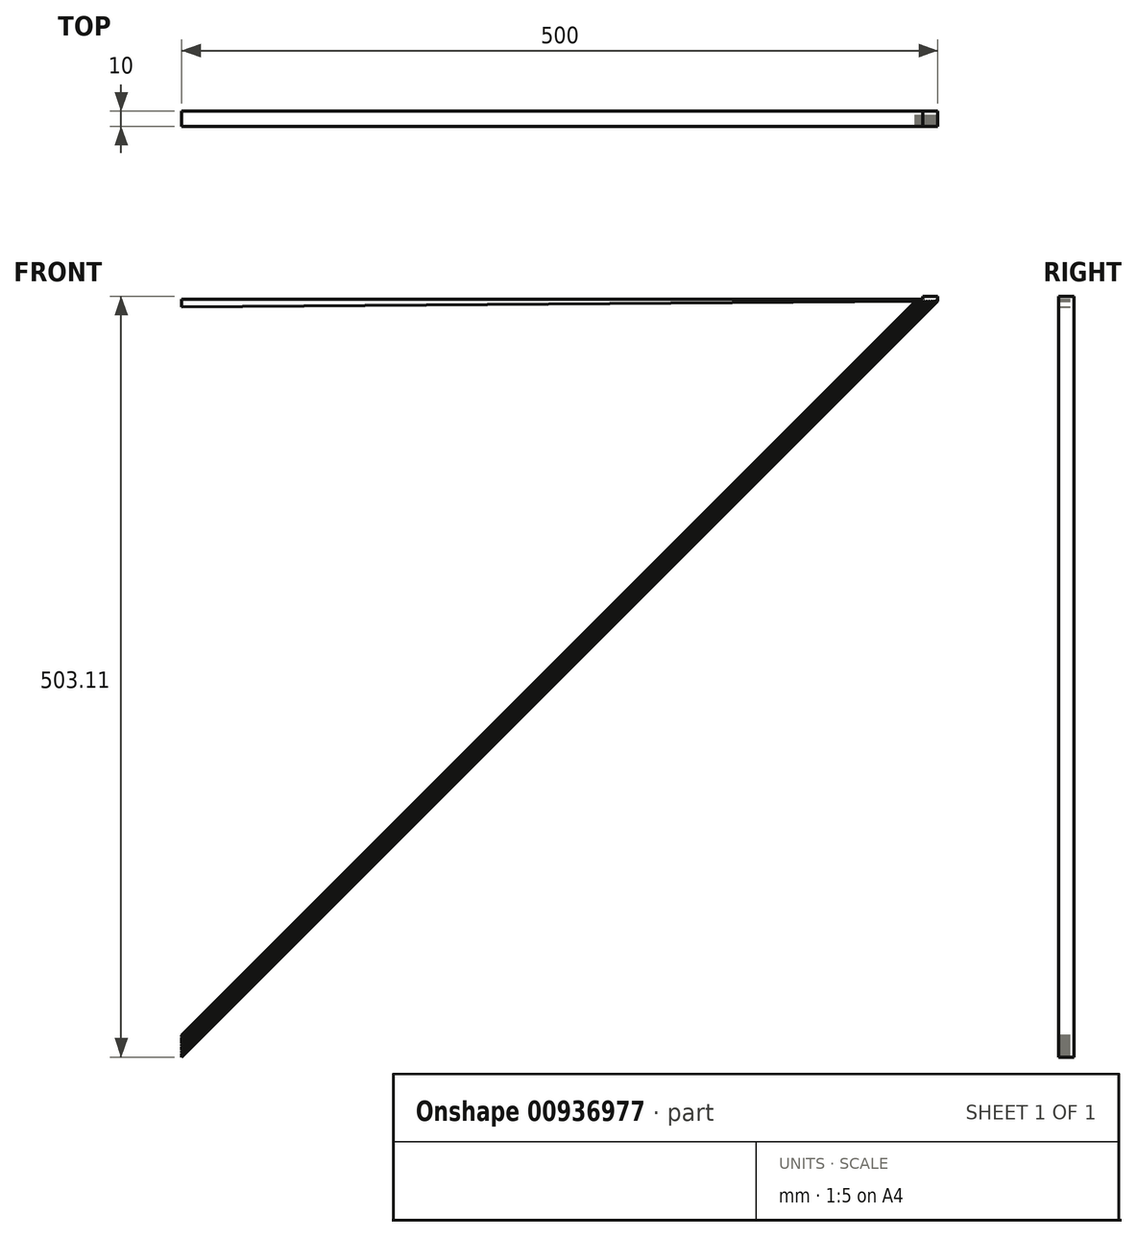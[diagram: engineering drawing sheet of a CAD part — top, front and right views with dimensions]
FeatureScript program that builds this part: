
annotation { "Feature Type Name" : "Feature", "Feature Type Description" : "" }
export const myFeature = defineFeature(function(context is Context, id is Id, definition is map)
    precondition{}
    {
        {
            var Q0;
            Q0=qCreatedBy(makeId("Front.planeOp"),FACE);
            var sketch = newSketch(context, id + "F0", { "sketchPlane" : qUnion([Q0])});
            skLineSegment(sketch, "E0.right", {"start": v(249.85, 318.38) * mm, "end": v(249.85, 317.38) * mm});
            skLineSegment(sketch, "E1", {"start": v(249.85, 318.38) * mm, "end": v(-250.15, 318.38) * mm});
            skLineSegment(sketch, "E2", {"start": v(-250.15, 318.38) * mm, "end": v(-250.15, 313.38) * mm});
            skLineSegment(sketch, "E3", {"start": v(249.85, 317.38) * mm, "end": v(-250.15, 313.38) * mm});
            skLineSegment(sketch, "E4", {"start": v(249.85, 317.38) * mm, "end": v(-250.15, -182.73) * mm});
            skLineSegment(sketch, "E5", {"start": v(249.85, 317.38) * mm, "end": v(248.85, 317.37) * mm});
            skLineSegment(sketch, "E6", {"start": v(248.85, 317.37) * mm, "end": v(248.35, 317.37) * mm});
            skLineSegment(sketch, "E7", {"start": v(248.35, 317.37) * mm, "end": v(247.35, 317.36) * mm});
            skLineSegment(sketch, "E8", {"start": v(-250.15, -182.73) * mm, "end": v(-250.15, -181.73) * mm});
            skLineSegment(sketch, "E9", {"start": v(-250.15, -181.73) * mm, "end": v(-250.15, -181.23) * mm});
            skLineSegment(sketch, "E10", {"start": v(-250.15, -181.23) * mm, "end": v(-250.15, -180.23) * mm});
            skLineSegment(sketch, "E11", {"start": v(248.85, 317.37) * mm, "end": v(-250.15, -181.73) * mm});
            skLineSegment(sketch, "E12", {"start": v(-250.15, -181.23) * mm, "end": v(248.35, 317.37) * mm});
            skLineSegment(sketch, "E13", {"start": v(247.35, 317.36) * mm, "end": v(-250.15, -180.23) * mm});
            skLineSegment(sketch, "E14", {"start": v(-250.15, -180.23) * mm, "end": v(-250.15, -179.73) * mm});
            skLineSegment(sketch, "E15", {"start": v(-250.15, -179.73) * mm, "end": v(-250.15, -178.73) * mm});
            skLineSegment(sketch, "E16", {"start": v(-250.15, -178.73) * mm, "end": v(-250.15, -178.23) * mm});
            skLineSegment(sketch, "E17", {"start": v(-250.15, -178.23) * mm, "end": v(-250.15, -177.23) * mm});
            skLineSegment(sketch, "E18", {"start": v(247.35, 317.36) * mm, "end": v(246.85, 317.36) * mm});
            skLineSegment(sketch, "E19", {"start": v(246.85, 317.36) * mm, "end": v(245.85, 317.35) * mm});
            skLineSegment(sketch, "E20", {"start": v(245.85, 317.35) * mm, "end": v(245.35, 317.34) * mm});
            skLineSegment(sketch, "E21", {"start": v(245.35, 317.34) * mm, "end": v(244.35, 317.34) * mm});
            skLineSegment(sketch, "E22", {"start": v(246.85, 317.36) * mm, "end": v(-250.15, -179.73) * mm});
            skLineSegment(sketch, "E23", {"start": v(-250.15, -178.73) * mm, "end": v(245.85, 317.35) * mm});
            skLineSegment(sketch, "E24", {"start": v(245.35, 317.34) * mm, "end": v(-250.15, -178.23) * mm});
            skLineSegment(sketch, "E25", {"start": v(-250.15, -177.23) * mm, "end": v(244.35, 317.34) * mm});
            skLineSegment(sketch, "E26", {"start": v(244.35, 317.34) * mm, "end": v(243.85, 317.33) * mm});
            skLineSegment(sketch, "E27", {"start": v(243.85, 317.33) * mm, "end": v(242.85, 317.32) * mm});
            skLineSegment(sketch, "E28", {"start": v(242.85, 317.32) * mm, "end": v(242.35, 317.32) * mm});
            skLineSegment(sketch, "E29", {"start": v(242.35, 317.32) * mm, "end": v(241.35, 317.31) * mm});
            skLineSegment(sketch, "E30", {"start": v(241.35, 317.31) * mm, "end": v(240.85, 317.3) * mm});
            skLineSegment(sketch, "E31", {"start": v(240.85, 317.3) * mm, "end": v(239.85, 317.3) * mm});
            skLineSegment(sketch, "E32", {"start": v(-250.15, -177.23) * mm, "end": v(-250.15, -176.73) * mm});
            skLineSegment(sketch, "E33", {"start": v(-250.15, -176.73) * mm, "end": v(-250.15, -175.73) * mm});
            skLineSegment(sketch, "E34", {"start": v(-250.15, -175.73) * mm, "end": v(-250.15, -175.23) * mm});
            skLineSegment(sketch, "E35", {"start": v(-250.15, -175.23) * mm, "end": v(-250.15, -174.23) * mm});
            skLineSegment(sketch, "E36", {"start": v(-250.15, -174.23) * mm, "end": v(-250.15, -173.73) * mm});
            skLineSegment(sketch, "E37", {"start": v(-250.15, -173.73) * mm, "end": v(-250.15, -172.73) * mm});
            skLineSegment(sketch, "E38", {"start": v(-250.15, -176.73) * mm, "end": v(243.85, 317.33) * mm});
            skLineSegment(sketch, "E39", {"start": v(242.85, 317.32) * mm, "end": v(-250.15, -175.73) * mm});
            skLineSegment(sketch, "E40", {"start": v(-250.15, -175.23) * mm, "end": v(242.35, 317.32) * mm});
            skLineSegment(sketch, "E41", {"start": v(241.35, 317.31) * mm, "end": v(-250.15, -174.23) * mm});
            skLineSegment(sketch, "E42", {"start": v(-250.15, -173.73) * mm, "end": v(240.85, 317.3) * mm});
            skLineSegment(sketch, "E43", {"start": v(239.85, 317.3) * mm, "end": v(-250.15, -172.73) * mm});
            skLineSegment(sketch, "E44", {"start": v(-250.15, -172.73) * mm, "end": v(-250.15, -172.23) * mm});
            skLineSegment(sketch, "E45", {"start": v(-250.15, -172.23) * mm, "end": v(-250.15, -171.23) * mm});
            skLineSegment(sketch, "E46", {"start": v(239.85, 317.3) * mm, "end": v(239.35, 317.3) * mm});
            skLineSegment(sketch, "E47", {"start": v(239.35, 317.3) * mm, "end": v(238.35, 317.29) * mm});
            skLineSegment(sketch, "E48", {"start": v(239.35, 317.3) * mm, "end": v(-250.15, -172.23) * mm});
            skLineSegment(sketch, "E49", {"start": v(-250.15, -171.23) * mm, "end": v(238.35, 317.29) * mm});
            skLineSegment(sketch, "E50", {"start": v(-250.15, -171.23) * mm, "end": v(-250.15, -170.73) * mm});
            skLineSegment(sketch, "E51", {"start": v(-250.15, -170.73) * mm, "end": v(-250.15, -169.73) * mm});
            skLineSegment(sketch, "E52", {"start": v(238.35, 317.29) * mm, "end": v(237.85, 317.28) * mm});
            skLineSegment(sketch, "E53", {"start": v(237.85, 317.28) * mm, "end": v(236.85, 317.28) * mm});
            skLineSegment(sketch, "E54", {"start": v(237.85, 317.28) * mm, "end": v(-250.15, -170.73) * mm});
            skLineSegment(sketch, "E55", {"start": v(-250.15, -169.73) * mm, "end": v(236.85, 317.28) * mm});
            skLineSegment(sketch, "E56", {"start": v(236.85, 317.28) * mm, "end": v(236.35, 317.27) * mm});
            skLineSegment(sketch, "E57", {"start": v(236.35, 317.27) * mm, "end": v(235.35, 317.26) * mm});
            skLineSegment(sketch, "E58", {"start": v(-250.15, -169.73) * mm, "end": v(-250.15, -169.23) * mm});
            skLineSegment(sketch, "E59", {"start": v(-250.15, -169.23) * mm, "end": v(-250.15, -168.23) * mm});
            skLineSegment(sketch, "E60", {"start": v(-250.15, -169.23) * mm, "end": v(236.35, 317.27) * mm});
            skLineSegment(sketch, "E61", {"start": v(235.35, 317.26) * mm, "end": v(-250.15, -168.23) * mm});
            skSolve(sketch);
        }
        {
            var Q0;
            {var subQ19=sQuery(id+"F0.wireOp",EDGE,"E0.right");Q0=makeQuery(id+"F0.imprint","IMPRINT",FACE,{"disambiguationData":[TD([[makeQuery(id+"F0.imprint","IMPRINT",EDGE,{"derivedFrom":subQ19}),-1.0]])]});}
            var Q1;
            Q1=makeQuery(id+"F0.imprint","IMPRINT",FACE,{"disambiguationData":[TD([[makeQuery(id+"F0.imprint","IMPRINT",EDGE,{"derivedFrom":sQuery(id+"F0.wireOp",EDGE,"E10")}),-1.0]])]});
            var Q2;
            {var subQ0=sQuery(id+"F0.wireOp",EDGE,"E4");Q2=makeQuery(id+"F0.imprint","IMPRINT",FACE,{"disambiguationData":[TD([[makeQuery(id+"F0.imprint","IMPRINT",EDGE,{"derivedFrom":subQ0}),-1.0]])]});}
            var Q3;
            Q3=makeQuery(id+"F0.imprint","IMPRINT",FACE,{"disambiguationData":[TD([[makeQuery(id+"F0.imprint","IMPRINT",EDGE,{"derivedFrom":sQuery(id+"F0.wireOp",EDGE,"E17")}),-1.0]])]});
            var Q4;
            Q4=makeQuery(id+"F0.imprint","IMPRINT",FACE,{"disambiguationData":[TD([[makeQuery(id+"F0.imprint","IMPRINT",EDGE,{"derivedFrom":sQuery(id+"F0.wireOp",EDGE,"E15")}),-1.0]])]});
            var Q5;
            Q5=makeQuery(id+"F0.imprint","IMPRINT",FACE,{"disambiguationData":[TD([[makeQuery(id+"F0.imprint","IMPRINT",EDGE,{"derivedFrom":sQuery(id+"F0.wireOp",EDGE,"E37")}),-1.0]])]});
            var Q6;
            Q6=makeQuery(id+"F0.imprint","IMPRINT",FACE,{"disambiguationData":[TD([[makeQuery(id+"F0.imprint","IMPRINT",EDGE,{"derivedFrom":sQuery(id+"F0.wireOp",EDGE,"E35")}),-1.0]])]});
            var Q7;
            Q7=makeQuery(id+"F0.imprint","IMPRINT",FACE,{"disambiguationData":[TD([[makeQuery(id+"F0.imprint","IMPRINT",EDGE,{"derivedFrom":sQuery(id+"F0.wireOp",EDGE,"E33")}),-1.0]])]});
            var Q8;
            Q8=makeQuery(id+"F0.imprint","IMPRINT",FACE,{"disambiguationData":[TD([[makeQuery(id+"F0.imprint","IMPRINT",EDGE,{"derivedFrom":sQuery(id+"F0.wireOp",EDGE,"E45")}),-1.0]])]});
            var Q9;
            Q9=makeQuery(id+"F0.imprint","IMPRINT",FACE,{"disambiguationData":[TD([[makeQuery(id+"F0.imprint","IMPRINT",EDGE,{"derivedFrom":sQuery(id+"F0.wireOp",EDGE,"E51")}),-1.0]])]});
            var Q10;
            Q10=makeQuery(id+"F0.imprint","IMPRINT",FACE,{"disambiguationData":[TD([[makeQuery(id+"F0.imprint","IMPRINT",EDGE,{"derivedFrom":sQuery(id+"F0.wireOp",EDGE,"E59")}),-1.0]])]});
            extrude(context, id + "F1", {"entities" : qUnion([Q0, Q1, Q2, Q3, Q4, Q5, Q6, Q7, Q8, Q9, Q10]), "endBound" : BoundingType.SYMMETRIC, "depth" : 10 * mm, "offsetDistance" : 25 * mm});
        }
        {
            var Q0;
            Q0=makeQuery(id+"F1.opExtrude","SWEPT_FACE",FACE,{"disambiguationData":[OSD([sQuery(id+"F0.wireOp",EDGE,"E1")])]});
            var sketch = newSketch(context, id + "F2", { "sketchPlane" : qUnion([Q0])});
            skLineSegment(sketch, "E62.left", {"start": v(249.85, -5) * mm, "end": v(249.85, 5) * mm});
            skSolve(sketch);
        }
        {
            var Q0;
            Q0=makeQuery(id+"F1.opExtrude","SWEPT_FACE",FACE,{"disambiguationData":[OSD([sQuery(id+"F0.wireOp",EDGE,"E1")])]});
            var sketch = newSketch(context, id + "F3", { "sketchPlane" : qUnion([Q0])});
            skLineSegment(sketch, "E63.bottom", {"start": v(249.85, -5) * mm, "end": v(239.85, -5) * mm});
            skLineSegment(sketch, "E63.top", {"start": v(249.85, 5) * mm, "end": v(239.85, 5) * mm});
            skLineSegment(sketch, "E63.left", {"start": v(249.85, -5) * mm, "end": v(249.85, 5) * mm});
            skLineSegment(sketch, "E63.right", {"start": v(239.85, -5) * mm, "end": v(239.85, 5) * mm});
            skSolve(sketch);
        }
        {
            var Q0;
            Q0=qSketchRegion(id+"F3",true);
            var Q1;
            Q1=qSketchRegion(id+"F2",true);
            extrude(context, id + "F4", {"entities" : qUnion([Q0, Q1]), "operationType" : NewBodyOperationType.ADD, "depth" : 2 * mm, "offsetDistance" : 25 * mm});
        }
        {
            var Q0;
            Q0=makeQuery(id+"F4.opExtrude","CAP_EDGE",EDGE,{"disambiguationData":[OSD([sQuery(id+"F3.wireOp",EDGE,"E63.right")])],"isStart":true});
            var Q1;
            Q1=makeQuery(id+"F1.opExtrude","SWEPT_EDGE",EDGE,{"disambiguationData":[OSD([sQuery(id+"F0.wireOp",EDGE,"E0.right"),sQuery(id+"F0.wireOp",EDGE,"E3"),sQuery(id+"F0.wireOp",EDGE,"E4")])]});
            fillet(context, id + "F5", {"entities" : qUnion([Q0, Q1]), "radius" : 0.5 * mm, "tangentPropagation" : true, "allowEdgeOverflow" : false});
        }
    });
